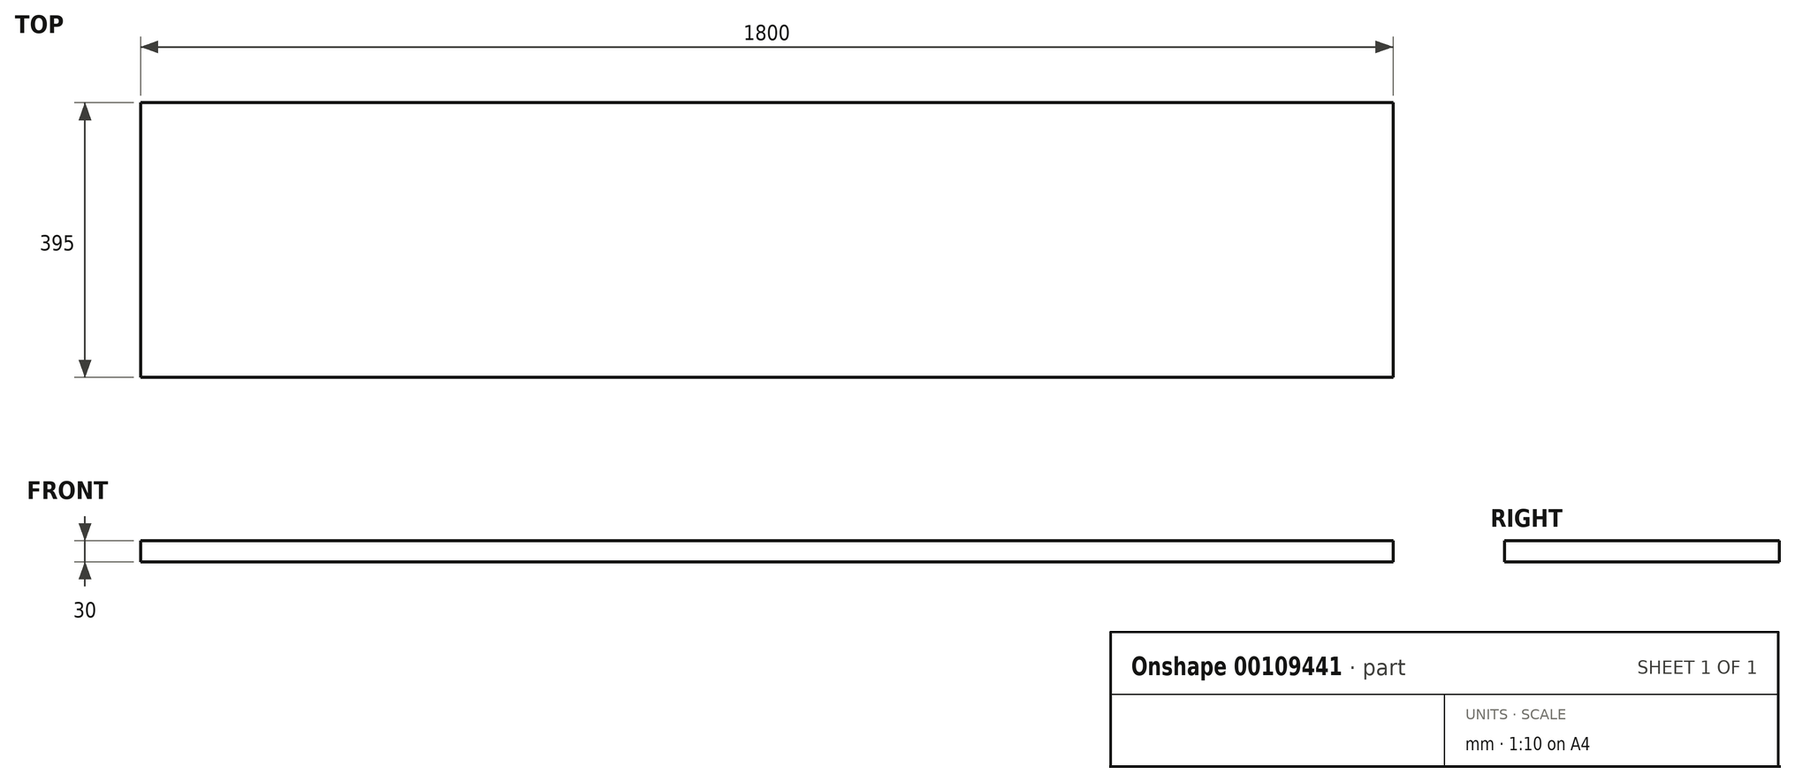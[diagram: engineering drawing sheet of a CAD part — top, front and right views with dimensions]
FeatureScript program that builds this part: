
annotation { "Feature Type Name" : "Feature", "Feature Type Description" : "" }
export const myFeature = defineFeature(function(context is Context, id is Id, definition is map)
    precondition{}
    {
        {
            var Q0;
            Q0=qCreatedBy(makeId("Top.planeOp"),FACE);
            var sketch = newSketch(context, id + "F0", { "sketchPlane" : qUnion([Q0])});
            skLineSegment(sketch, "E0.bottom", {"start": v(-900, 197.5) * mm, "end": v(900, 197.5) * mm});
            skLineSegment(sketch, "E0.top", {"start": v(-900, -197.5) * mm, "end": v(900, -197.5) * mm});
            skLineSegment(sketch, "E0.left", {"start": v(-900, 197.5) * mm, "end": v(-900, -197.5) * mm});
            skLineSegment(sketch, "E0.right", {"start": v(900, 197.5) * mm, "end": v(900, -197.5) * mm});
            skLineSegment(sketch, "E1", {"start": v(-900, 197.5) * mm, "end": v(900, -197.5) * mm, "construction": true});
            skSolve(sketch);
        }
        {
            var Q0;
            Q0 = qSketchRegion(id + "F0", true);
            extrude(context, id + "F1", {"entities" : qUnion([Q0]), "depth" : 30 * mm});
        }
    });
